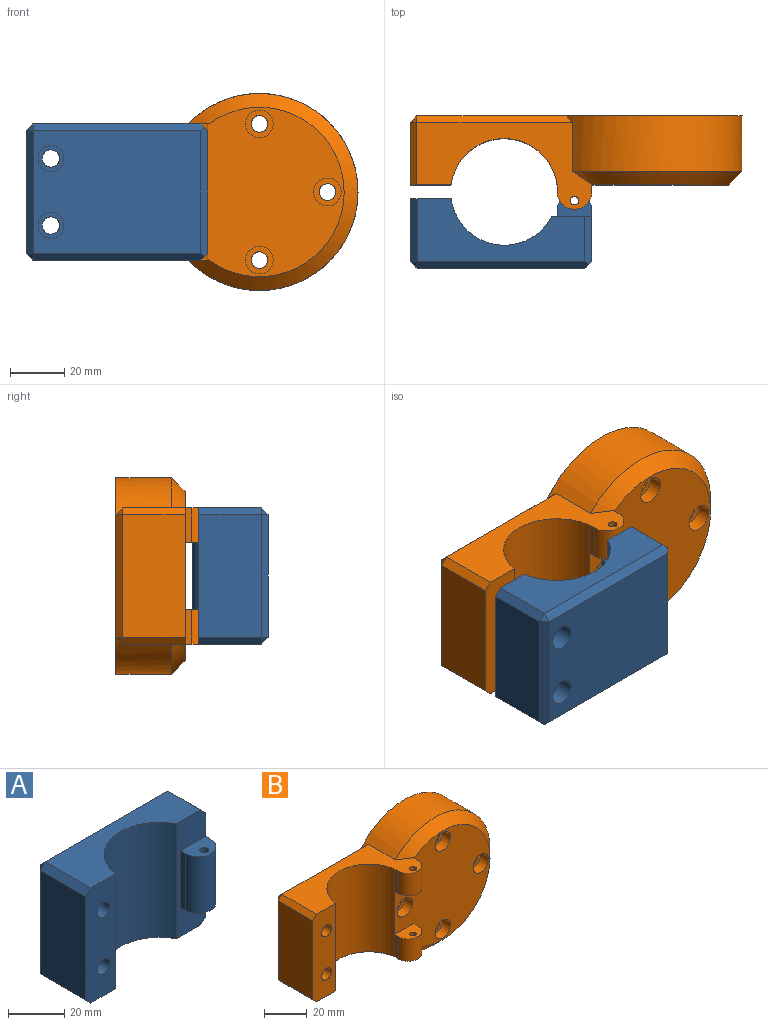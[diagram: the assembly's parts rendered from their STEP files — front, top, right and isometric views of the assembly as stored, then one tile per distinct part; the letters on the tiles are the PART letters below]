
ASSEMBLY  parts=2 mates=1
PART A: 29 faces, bbox 66.7x27.9x50 mm
  f0: plane 44.96x19.05mm, normal (1,0,0), area 804.8mm2, adj f2,f4,f5,f17,f18,f19,f20
  f1: plane 61.6x22.86mm, normal (0,0,1), area 833.9mm2, adj f4,f6,f11,f17,f26,f28
  f2: cylinder r=6.35mm len=24.64mm, axis (0,0,-1), area 491.5mm2, adj f0,f3,f19,f20
  f3: plane 24.64x2.54mm, normal (-1,0,0), area 62.6mm2, adj f2,f17,f19,f20
  f4: plane 17.78x2.54mm, normal (0.71,0,0.71), area 61.6mm2, adj f0,f1,f17,f18,f26
  f5: plane 17.78x2.54mm, normal (0.71,0,-0.71), area 61.6mm2, adj f0,f9,f17,f18,f23
  f6: cylinder r=19.69mm len=50.04mm, axis (0,0,-1), area 2494.8mm2, adj f1,f9,f11,f17
  f7: cylinder r=3.17mm len=19.05mm, axis (0,-1,0), area 380mm2, adj f11,f15
  f8: cylinder r=3.17mm len=19.05mm, axis (0,-1,0), area 380mm2, adj f11,f13
  f9: plane 61.6x22.86mm, normal (0,0,-1), area 833.9mm2, adj f5,f6,f11,f17,f22,f23
  f10: plane 61.6x44.96mm, normal (0,1,0), area 2626.7mm2, adj f12,f14,f18,f23,f25,f26
  f11: plane 50.04x15.04mm, normal (0,-1,0), area 682.6mm2, adj f1,f6,f7,f8,f9,f16,f22,f28
  f12: cylinder r=4.76mm len=9.53mm, axis (0,1,0), area 190mm2, adj f10,f13
  f13: plane 9.53x9.53mm, normal (0,1,0), area 39.6mm2, adj f8,f12
  f14: cylinder r=4.76mm len=9.53mm, axis (0,1,0), area 190mm2, adj f10,f15
  f15: plane 9.53x9.53mm, normal (0,1,0), area 39.6mm2, adj f7,f14
  f16: plane 44.96x22.86mm, normal (-1,0,0), area 1027.7mm2, adj f11,f22,f25,f28
  f17: plane 50.04x14.62mm, normal (0,-1,0), area 412.1mm2, adj f0,f1,f3,f4,f5,f6,f9,f19
  f18: plane 47.5x2.54mm, normal (0.71,0.71,0), area 166.1mm2, adj f0,f4,f5,f10,f23,f26
  f19: plane 12.7x8.89mm, normal (0,0,-1), area 87.7mm2, adj f0,f2,f3,f17,f21
  f20: plane 12.7x8.89mm, normal (0,0,1), area 87.7mm2, adj f0,f2,f3,f17,f21
  f21: cylinder r=1.59mm len=24.64mm, axis (0,0,-1), area 245.8mm2, adj f19,f20
  f22: plane 22.86x2.54mm, normal (-0.71,0,-0.71), area 82.1mm2, adj f9,f11,f16,f24
  f23: plane 62.87x2.54mm, normal (0,0.71,-0.71), area 223.5mm2, adj f5,f9,f10,f18,f24
  f24: plane 2.54x2.54mm, normal (-0.58,0.58,-0.58), area 5.6mm2, adj f22,f23,f25
  f25: plane 44.96x2.54mm, normal (-0.71,0.71,0), area 161.5mm2, adj f10,f16,f24,f27
  f26: plane 62.87x2.54mm, normal (0,0.71,0.71), area 223.5mm2, adj f1,f4,f10,f18,f27
  f27: plane 2.54x2.54mm, normal (-0.58,0.58,0.58), area 5.6mm2, adj f25,f26,f28
  f28: plane 22.86x2.54mm, normal (-0.71,0,0.71), area 82.1mm2, adj f1,f11,f16,f27
PART B: 44 faces, bbox 122x34.3x72.4 mm
  f0: cylinder r=3.05mm len=13.82mm, axis (0,-1,0), area 264.6mm2, adj f11,f27
  f1: cylinder r=3.05mm len=13.82mm, axis (0,-1,0), area 264.6mm2, adj f11,f25
  f2: cylinder r=3.05mm len=13.82mm, axis (0,-1,0), area 264.6mm2, adj f11,f23
  f3: cylinder r=3.05mm len=13.82mm, axis (0,-1,0), area 264.6mm2, adj f11,f21
  f4: plane 12.7x2.54mm, normal (-1,0,0), area 32.3mm2, adj f6,f13,f14,f17
  f5: plane 62.79x62.23mm, normal (0,-1,0), area 2612.1mm2, adj f12,f13,f15,f17,f22,f24,f26,f28
  f6: plane 64.21x31.75mm, normal (0,0,-1), area 905.1mm2, adj f4,f7,f8,f13,f14,f15,f16,f29
  f7: cylinder r=36.2mm len=72.39mm, axis (0,1,0), area 3507.1mm2, adj f6,f9,f12,f29,f38,f41
  f8: plane 50.04x15.04mm, normal (0,-1,0), area 682.8mm2, adj f6,f12,f13,f18,f19,f20,f37,f43
  f9: plane 119.38x72.39mm, normal (0,1,0), area 3109.7mm2, adj f7,f10,f18,f19,f38,f40,f41
  f10: cylinder r=31.75mm len=63.5mm, axis (0,1,0), area 1297.2mm2, adj f9,f11
  f11: plane 63.5x63.5mm, normal (0,1,0), area 2271.1mm2, adj f0,f1,f2,f3,f10,f30
  f12: plane 64.69x31.75mm, normal (0,0,1), area 905.1mm2, adj f5,f7,f8,f13,f29,f32,f33,f34
  f13: cylinder r=19.69mm len=50.04mm, axis (0,0,-1), area 2829.5mm2, adj f4,f5,f6,f8,f12,f32
  f14: cylinder r=6.35mm len=12.7mm, axis (0,0,-1), area 253.4mm2, adj f4,f6,f15,f17
  f15: plane 12.7x2.82mm, normal (1,0,0), area 32.3mm2, adj f5,f6,f14,f17,f29
  f16: cylinder r=1.59mm len=12.7mm, axis (0,0,-1), area 126.7mm2, adj f6,f17
  f17: plane 12.7x8.89mm, normal (0,0,1), area 87.7mm2, adj f4,f5,f14,f15,f16
  f18: cylinder r=3.17mm len=25.4mm, axis (0,-1,0), area 506.7mm2, adj f8,f9
  f19: cylinder r=3.17mm len=25.4mm, axis (0,-1,0), area 506.7mm2, adj f8,f9
  f20: plane 44.96x22.86mm, normal (-1,0,0), area 1027.7mm2, adj f8,f37,f40,f43
  f21: plane 10.16x10.16mm, normal (0,-1,0), area 51.9mm2, adj f3,f22
  f22: cylinder r=5.08mm len=10.16mm, axis (0,-1,0), area 162.1mm2, adj f5,f21
  f23: plane 10.16x10.16mm, normal (0,-1,0), area 51.9mm2, adj f2,f24
  f24: cylinder r=5.08mm len=10.16mm, axis (0,-1,0), area 162.1mm2, adj f5,f23
  f25: plane 10.16x10.16mm, normal (0,-1,0), area 51.9mm2, adj f1,f26
  f26: cylinder r=5.08mm len=10.16mm, axis (0,-1,0), area 162.1mm2, adj f5,f25
  f27: plane 10.16x10.16mm, normal (0,-1,0), area 51.9mm2, adj f0,f28
  f28: cylinder r=5.08mm len=10.16mm, axis (0,-1,0), area 162.1mm2, adj f5,f27
  f29: cone r=31.12mm half-angle=45deg, axis (0,1,0), area 1113.4mm2, adj f5,f6,f7,f12,f15
  f30: cylinder r=15.75mm len=31.5mm, axis (0,-1,0), area 628.3mm2, adj f11,f31
  f31: plane 31.5x31.5mm, normal (0,1,0), area 779.1mm2, adj f30
  f32: plane 12.7x2.54mm, normal (-1,0,0), area 32.3mm2, adj f12,f13,f33,f36
  f33: cylinder r=6.35mm len=12.7mm, axis (0,0,1), area 253.4mm2, adj f12,f32,f34,f36
  f34: plane 12.7x2.54mm, normal (1,0,0), area 32.3mm2, adj f5,f12,f33,f36
  f35: cylinder r=1.59mm len=12.7mm, axis (0,0,1), area 126.7mm2, adj f12,f36
  f36: plane 12.7x8.89mm, normal (0,0,-1), area 87.7mm2, adj f5,f32,f33,f34,f35
  f37: plane 22.86x2.54mm, normal (-0.71,0,-0.71), area 82.1mm2, adj f6,f8,f20,f39
  f38: plane 57.08x2.59mm, normal (0,0.71,-0.71), area 200.8mm2, adj f6,f7,f9,f39
  f39: plane 2.54x2.54mm, normal (-0.58,0.58,-0.58), area 5.6mm2, adj f37,f38,f40
  f40: plane 44.96x2.54mm, normal (-0.71,0.71,0), area 161.5mm2, adj f9,f20,f39,f42
  f41: plane 57.08x2.59mm, normal (0,0.71,0.71), area 200.8mm2, adj f7,f9,f12,f42
  f42: plane 2.54x2.54mm, normal (-0.58,0.58,0.58), area 5.6mm2, adj f40,f41,f43
  f43: plane 22.86x2.54mm, normal (-0.71,0,0.71), area 82.1mm2, adj f8,f12,f20,f42
PLACE A rot(axis=(1,0,0),180deg) t=(295.45,-0.06,200.35)mm
PLACE B t=(334.59,4.52,170.89)mm
MATE fastened A.f21 <-> B.f16  axis (0,0,1) through (59.4,-26.59,163.01)mm
